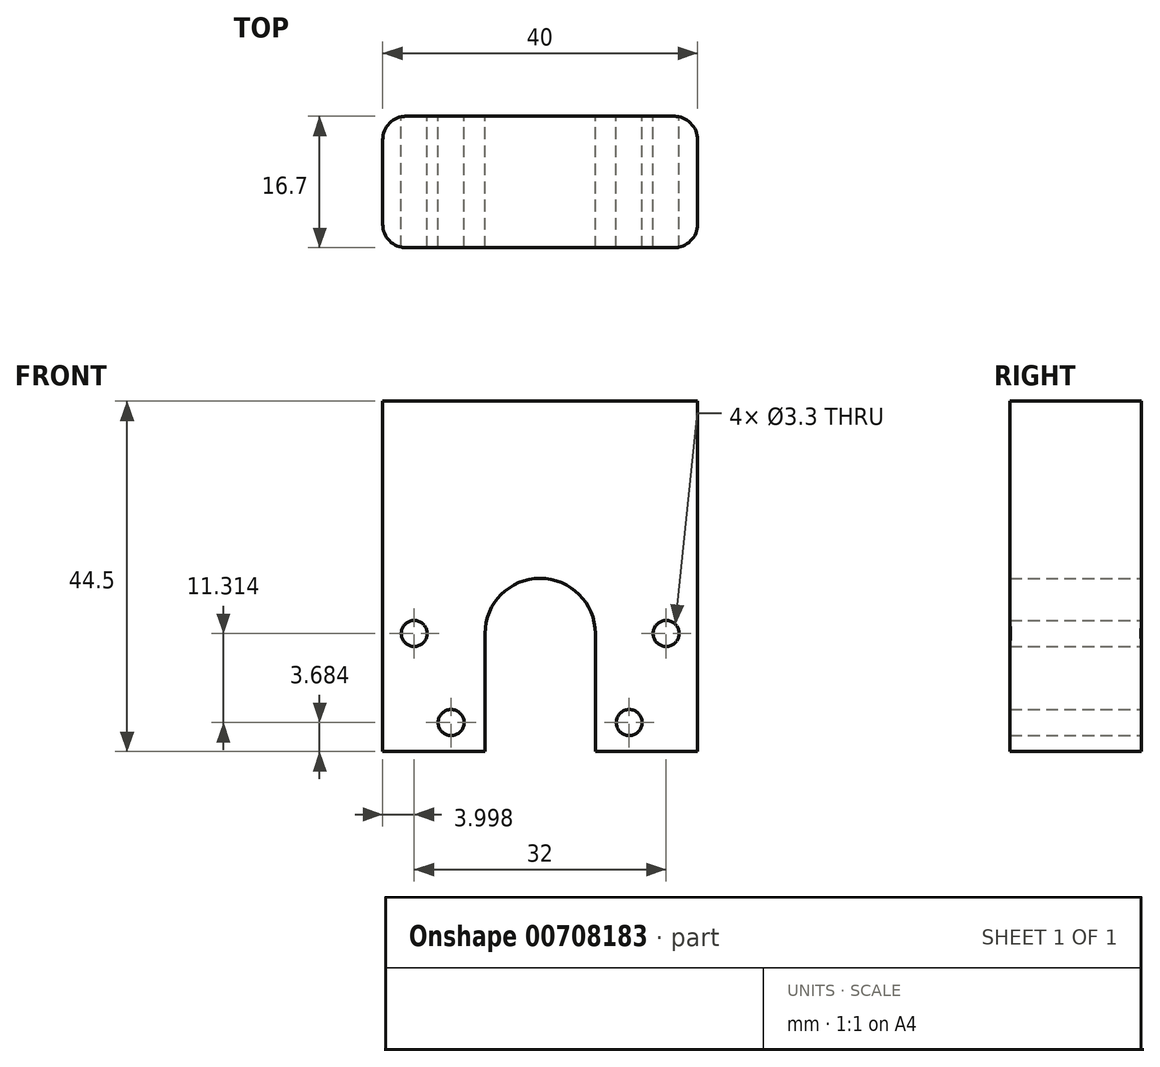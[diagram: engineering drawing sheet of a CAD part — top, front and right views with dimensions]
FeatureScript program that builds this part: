
annotation { "Feature Type Name" : "Feature", "Feature Type Description" : "" }
export const myFeature = defineFeature(function(context is Context, id is Id, definition is map)
    precondition{}
    {
        {
            var Q0;
            Q0=qCreatedBy(makeId("Front.planeOp"),FACE);
            var sketch = newSketch(context, id + "F0", { "sketchPlane" : qUnion([Q0])});
            skLineSegment(sketch, "E0.bottom", {"start": v(-19.28, 16.73) * mm, "end": v(20.72, 16.73) * mm});
            skLineSegment(sketch, "E0.top", {"start": v(-19.28, -27.77) * mm, "end": v(-6.28, -27.77) * mm});
            skLineSegment(sketch, "E0.left", {"start": v(-19.28, 16.73) * mm, "end": v(-19.28, -27.77) * mm});
            skLineSegment(sketch, "E0.right", {"start": v(20.72, 16.73) * mm, "end": v(20.72, -27.77) * mm});
            skLineSegment(sketch, "E1", {"start": v(0.72, 16.73) * mm, "end": v(0.72, -27.77) * mm, "construction": true});
            skLineSegment(sketch, "E2", {"start": v(0.72, -12.77) * mm, "end": v(-15.28, -12.77) * mm, "construction": true});
            skCircle(sketch, "E3", {"center": v(-15.28, -12.77) * mm, "radius": 1.65 * mm});
            skCircle(sketch, "E4.0.MirrorC", {"center": v(16.72, -12.77) * mm, "radius": 1.65 * mm});
            skArc(sketch, "E5", {"start": v(7.72, -12.77) * mm, "mid": v(0.72, -5.77) * mm, "end": v(-6.28, -12.77) * mm});
            skLineSegment(sketch, "E6", {"start": v(-6.28, -12.77) * mm, "end": v(-6.28, -27.77) * mm});
            skLineSegment(sketch, "E7", {"start": v(7.72, -12.77) * mm, "end": v(7.72, -27.77) * mm});
            skLineSegment(sketch, "E8.trimOffspring", {"start": v(7.72, -27.77) * mm, "end": v(20.72, -27.77) * mm});
            skLineSegment(sketch, "E9", {"start": v(0.72, -12.77) * mm, "end": v(0.72, 16.73) * mm, "construction": true});
            skLineSegment(sketch, "E10", {"start": v(20.72, -3.27) * mm, "end": v(-19.28, -3.27) * mm, "construction": true});
            skLineSegment(sketch, "E11", {"start": v(20.72, -4.77) * mm, "end": v(-19.28, -4.77) * mm, "construction": true});
            skCircle(sketch, "E12.1.0", {"center": v(-10.6, -24.09) * mm, "radius": 1.65 * mm});
            skLineSegment(sketch, "E12.anchor2", {"start": v(0.72, -12.77) * mm, "end": v(-10.6, -24.09) * mm, "construction": true});
            skCircle(sketch, "E13.0.MirrorC", {"center": v(12.03, -24.09) * mm, "radius": 1.65 * mm});
            skLineSegment(sketch, "E14", {"start": v(-9.88, -5.77) * mm, "end": v(14.62, -5.77) * mm, "construction": true});
            skSolve(sketch);
        }
        {
            var Q0;
            Q0=qSketchRegion(id+"F0",true);
            extrude(context, id + "F1", {"entities" : qUnion([Q0]), "depth" : 16.7 * mm});
        }
        {
            var Q0;
            Q0=makeQuery(id+"F1.opExtrude","CAP_EDGE",EDGE,{"disambiguationData":[OSD([sQuery(id+"F0.wireOp",EDGE,"E0.left")])],"isStart":false});
            var Q1;
            Q1=makeQuery(id+"F1.opExtrude","CAP_EDGE",EDGE,{"disambiguationData":[OSD([sQuery(id+"F0.wireOp",EDGE,"E0.right")])],"isStart":false});
            var Q2;
            Q2=makeQuery(id+"F1.opExtrude","CAP_EDGE",EDGE,{"disambiguationData":[OSD([sQuery(id+"F0.wireOp",EDGE,"E0.right")])],"isStart":true});
            var Q3;
            Q3=makeQuery(id+"F1.opExtrude","CAP_EDGE",EDGE,{"disambiguationData":[OSD([sQuery(id+"F0.wireOp",EDGE,"E0.left")])],"isStart":true});
            fillet(context, id + "F2", {"entities" : qUnion([Q0, Q1, Q2, Q3]), "radius" : 3 * mm, "tangentPropagation" : true, "allowEdgeOverflow" : false});
        }
    });
